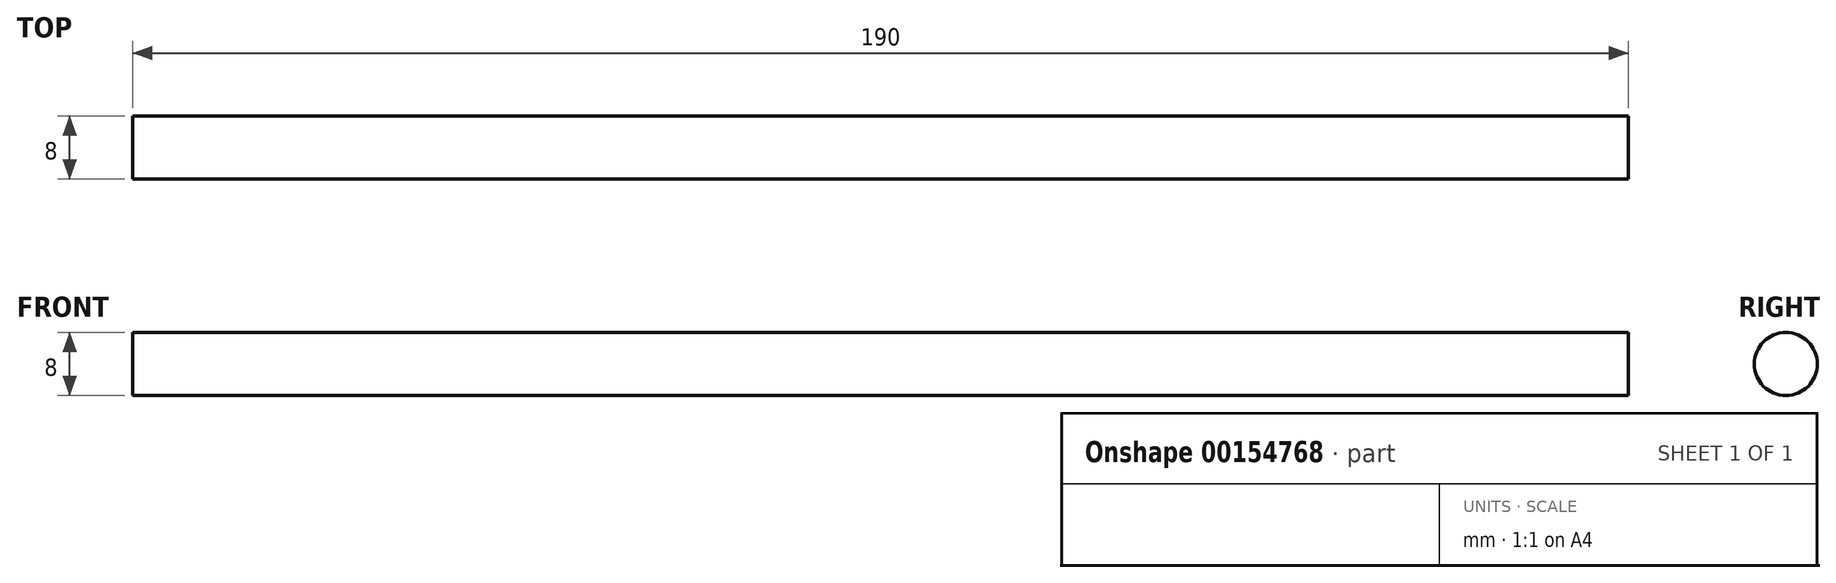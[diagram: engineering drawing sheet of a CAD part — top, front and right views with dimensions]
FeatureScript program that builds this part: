
annotation { "Feature Type Name" : "Feature", "Feature Type Description" : "" }
export const myFeature = defineFeature(function(context is Context, id is Id, definition is map)
    precondition{}
    {
        {
            var Q0;
            Q0=qCreatedBy(makeId("Right.planeOp"),FACE);
            var sketch = newSketch(context, id + "F0", { "sketchPlane" : qUnion([Q0])});
            skCircle(sketch, "E0", {"center": v(0, 0) * mm, "radius": 4 * mm});
            skSolve(sketch);
        }
        {
            var Q0;
            Q0 = qSketchRegion(id + "F0", true);
            extrude(context, id + "F1", {"entities" : qUnion([Q0]), "depth" : 190 * mm, "symmetric" : true});
        }
    });
